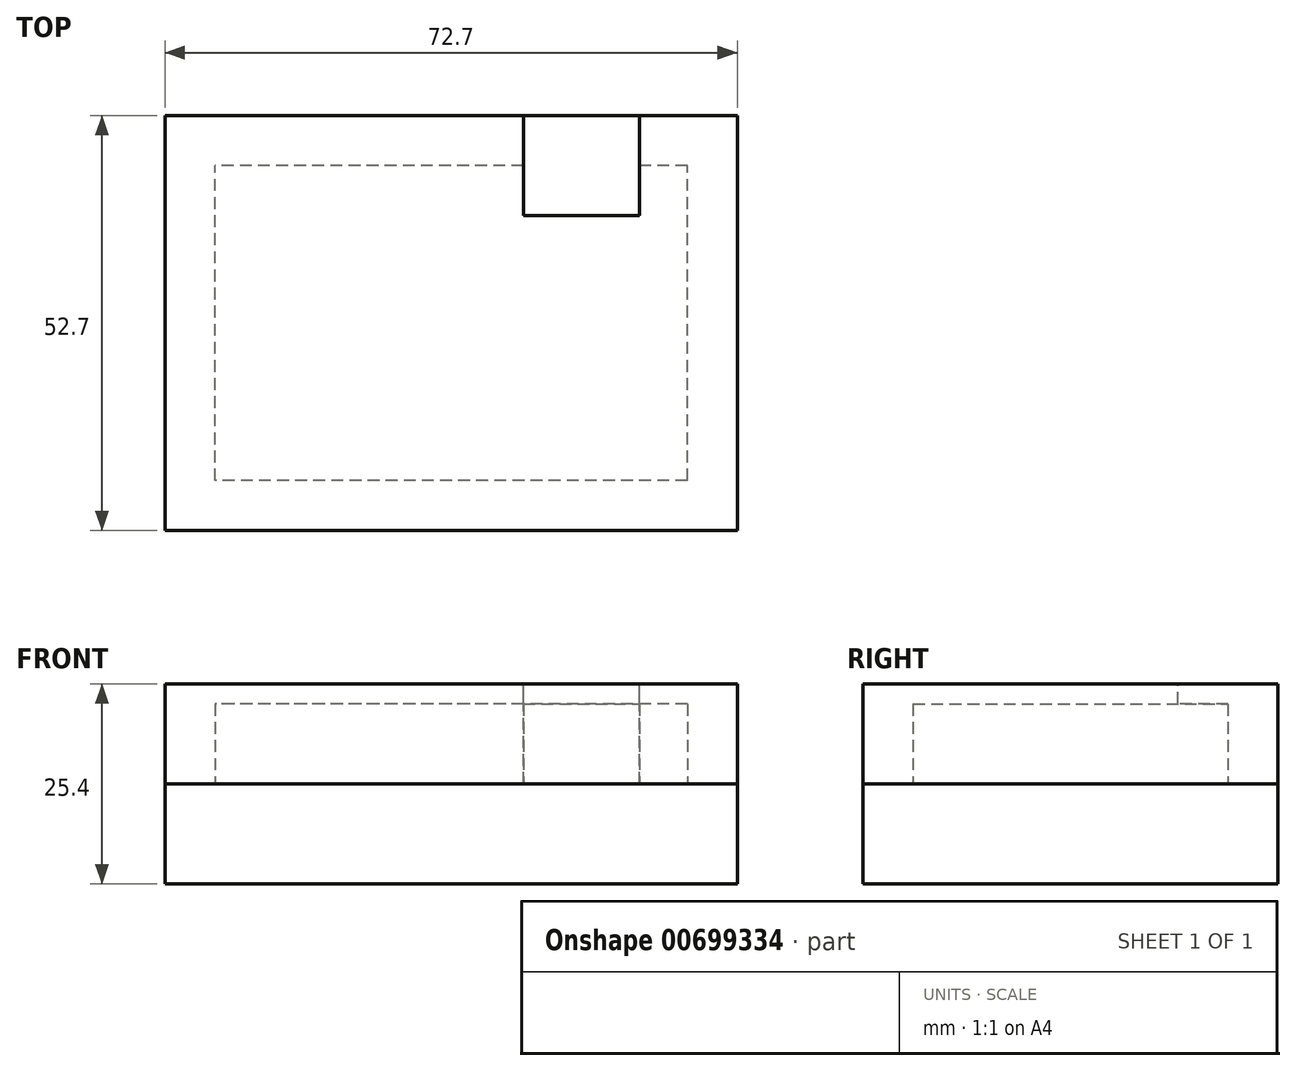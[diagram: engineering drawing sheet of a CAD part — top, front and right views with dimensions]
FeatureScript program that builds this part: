
annotation { "Feature Type Name" : "Feature", "Feature Type Description" : "" }
export const myFeature = defineFeature(function(context is Context, id is Id, definition is map)
    precondition{}
    {
        {
            var Q0;
            Q0=qCreatedBy(makeId("Top.planeOp"),FACE);
            var sketch = newSketch(context, id + "F0", { "sketchPlane" : qUnion([Q0])});
            skLineSegment(sketch, "E0.bottom", {"start": v(30, -20) * mm, "end": v(-30, -20) * mm, "construction": true});
            skLineSegment(sketch, "E0.top", {"start": v(30, 20) * mm, "end": v(-30, 20) * mm, "construction": true});
            skLineSegment(sketch, "E0.left", {"start": v(30, -20) * mm, "end": v(30, 20) * mm, "construction": true});
            skLineSegment(sketch, "E0.right", {"start": v(-30, -20) * mm, "end": v(-30, 20) * mm, "construction": true});
            skPoint(sketch, "E0.middle", {"position": v(0, 0) * mm});
            skLineSegment(sketch, "E1.0", {"start": v(30, 26.35) * mm, "end": v(-30, 26.35) * mm});
            skLineSegment(sketch, "E2.0", {"start": v(36.35, -26.35) * mm, "end": v(36.35, 26.35) * mm});
            skLineSegment(sketch, "E2.1", {"start": v(36.35, -26.35) * mm, "end": v(-36.35, -26.35) * mm});
            skLineSegment(sketch, "E2.2", {"start": v(-36.35, -26.35) * mm, "end": v(-36.35, 26.35) * mm});
            skLineSegment(sketch, "E2.3", {"start": v(36.35, 26.35) * mm, "end": v(-36.35, 26.35) * mm});
            skSolve(sketch);
        }
        {
            var Q0;
            Q0 = qSketchRegion(id + "F0", true);
            extrude(context, id + "F1", {"entities" : qUnion([Q0]), "depth" : 12.7 * mm, "offsetDistance" : 25.4 * mm});
        }
        {
            var Q0;
            Q0=makeQuery(id+"F1.opExtrude","CAP_FACE",FACE,{"disambiguationData":[OSD([sQuery(id+"F0.wireOp",EDGE,"E2.0"),sQuery(id+"F0.wireOp",EDGE,"E2.1"),sQuery(id+"F0.wireOp",EDGE,"E2.2"),sQuery(id+"F0.wireOp",EDGE,"E2.3")])],"isStart":true});
            var sketch = newSketch(context, id + "F2", { "sketchPlane" : qUnion([Q0])});
            skPoint(sketch, "E3.0", {"position": v(-30, 20) * mm});
            skLineSegment(sketch, "E3.1", {"start": v(-30, 20) * mm, "end": v(-30, -20) * mm});
            skPoint(sketch, "E3.2", {"position": v(-30, -20) * mm});
            skLineSegment(sketch, "E3.3", {"start": v(30, -20) * mm, "end": v(-30, -20) * mm});
            skLineSegment(sketch, "E3.4", {"start": v(30, 20) * mm, "end": v(30, -20) * mm});
            skPoint(sketch, "E3.5", {"position": v(30, -20) * mm});
            skPoint(sketch, "E3.6", {"position": v(30, 20) * mm});
            skLineSegment(sketch, "E3.7", {"start": v(30, 20) * mm, "end": v(-30, 20) * mm});
            skSolve(sketch);
        }
        {
            var Q0;
            Q0 = qSketchRegion(id + "F2", true);
            var Q1;
            Q1=makeQuery(id+"F1.opExtrude","CAP_FACE",FACE,{"disambiguationData":[OSD([sQuery(id+"F0.wireOp",EDGE,"E2.0"),sQuery(id+"F0.wireOp",EDGE,"E2.1"),sQuery(id+"F0.wireOp",EDGE,"E2.2"),sQuery(id+"F0.wireOp",EDGE,"E2.3")])],"isStart":false});
            extrude(context, id + "F3", {"entities" : qUnion([Q0]), "operationType" : NewBodyOperationType.REMOVE, "endBound" : BoundingType.UP_TO_SURFACE, "oppositeDirection" : true, "depth" : 25.4 * mm, "endBoundEntityFace" : qUnion([Q1]), "hasOffset" : true, "offsetDistance" : 2.54 * mm});
        }
        {
            var Q0;
            Q0=makeQuery(id+"F1.opExtrude","CAP_FACE",FACE,{"disambiguationData":[OSD([sQuery(id+"F0.wireOp",EDGE,"E2.0"),sQuery(id+"F0.wireOp",EDGE,"E2.1"),sQuery(id+"F0.wireOp",EDGE,"E2.2"),sQuery(id+"F0.wireOp",EDGE,"E2.3")])],"isStart":false});
            var sketch = newSketch(context, id + "F4", { "sketchPlane" : qUnion([Q0])});
            skLineSegment(sketch, "E4.bottom", {"start": v(9.17, 26.35) * mm, "end": v(23.9, 26.35) * mm});
            skLineSegment(sketch, "E4.top", {"start": v(9.17, 13.65) * mm, "end": v(23.9, 13.65) * mm});
            skLineSegment(sketch, "E4.left", {"start": v(9.17, 26.35) * mm, "end": v(9.17, 13.65) * mm});
            skLineSegment(sketch, "E4.right", {"start": v(23.9, 26.35) * mm, "end": v(23.9, 13.65) * mm});
            skPoint(sketch, "E5.0", {"position": v(30, 0) * mm});
            skSolve(sketch);
        }
        {
            var Q0;
            Q0 = qSketchRegion(id + "F4", true);
            var Q1;
            Q1=makeQuery(id+"F1.opExtrude","CAP_FACE",FACE,{"disambiguationData":[OSD([sQuery(id+"F0.wireOp",EDGE,"E2.0"),sQuery(id+"F0.wireOp",EDGE,"E2.1"),sQuery(id+"F0.wireOp",EDGE,"E2.2"),sQuery(id+"F0.wireOp",EDGE,"E2.3")])],"isStart":true});
            extrude(context, id + "F5", {"entities" : qUnion([Q0]), "operationType" : NewBodyOperationType.REMOVE, "endBound" : BoundingType.UP_TO_SURFACE, "oppositeDirection" : true, "depth" : 25.4 * mm, "endBoundEntityFace" : qUnion([Q1]), "offsetDistance" : 25.4 * mm});
        }
        {
            var Q0;
            Q0=makeQuery(id+"F1.opExtrude","CAP_FACE",FACE,{"disambiguationData":[OSD([sQuery(id+"F0.wireOp",EDGE,"E2.0"),sQuery(id+"F0.wireOp",EDGE,"E2.1"),sQuery(id+"F0.wireOp",EDGE,"E2.2"),sQuery(id+"F0.wireOp",EDGE,"E2.3")])],"isStart":true});
            var sketch = newSketch(context, id + "F6", { "sketchPlane" : qUnion([Q0])});
            skLineSegment(sketch, "E6.bottom", {"start": v(-36.35, 26.35) * mm, "end": v(36.35, 26.35) * mm});
            skLineSegment(sketch, "E6.top", {"start": v(-36.35, -26.35) * mm, "end": v(36.35, -26.35) * mm});
            skLineSegment(sketch, "E6.left", {"start": v(-36.35, 26.35) * mm, "end": v(-36.35, -26.35) * mm});
            skLineSegment(sketch, "E6.right", {"start": v(36.35, 26.35) * mm, "end": v(36.35, -26.35) * mm});
            skSolve(sketch);
        }
        {
            var Q0;
            Q0 = qSketchRegion(id + "F6", true);
            extrude(context, id + "F7", {"entities" : qUnion([Q0]), "depth" : 12.7 * mm, "offsetDistance" : 25.4 * mm});
        }
    });
